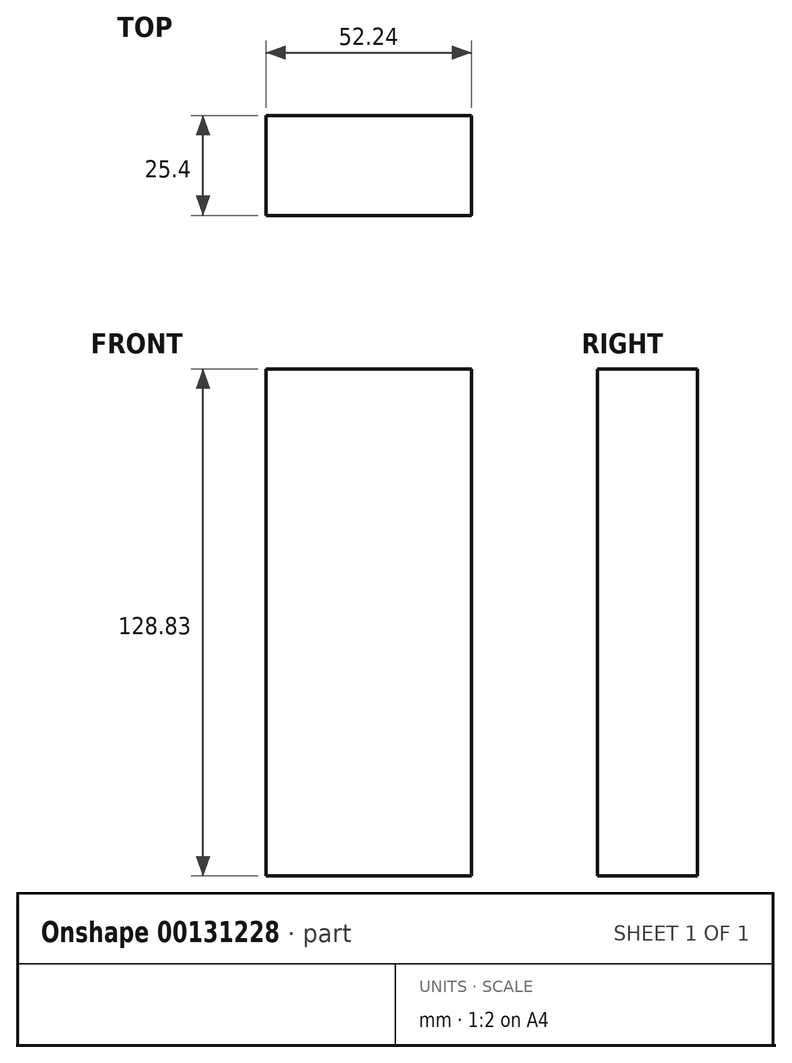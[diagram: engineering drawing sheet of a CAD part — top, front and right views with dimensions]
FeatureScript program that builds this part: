
annotation { "Feature Type Name" : "Feature", "Feature Type Description" : "" }
export const myFeature = defineFeature(function(context is Context, id is Id, definition is map)
    precondition{}
    {
        {
            var Q0;
            Q0=qCreatedBy(makeId("Front.planeOp"),FACE);
            var sketch = newSketch(context, id + "F0", { "sketchPlane" : qUnion([Q0])});
            skLineSegment(sketch, "E0.bottom", {"start": v(-30.38, -8.5) * mm, "end": v(-82.62, -8.5) * mm});
            skLineSegment(sketch, "E0.top", {"start": v(-30.38, 120.33) * mm, "end": v(-82.62, 120.33) * mm});
            skLineSegment(sketch, "E0.left", {"start": v(-30.38, -8.5) * mm, "end": v(-30.38, 120.33) * mm});
            skLineSegment(sketch, "E0.right", {"start": v(-82.62, -8.5) * mm, "end": v(-82.62, 120.33) * mm});
            skPoint(sketch, "E0.middle", {"position": v(-56.5, 55.91) * mm});
            skLineSegment(sketch, "E1.bottom", {"start": v(15.98, -28.7) * mm, "end": v(-4.11, -28.7) * mm});
            skLineSegment(sketch, "E1.top", {"start": v(15.98, 110.48) * mm, "end": v(-4.11, 110.48) * mm});
            skLineSegment(sketch, "E1.left", {"start": v(15.98, -28.7) * mm, "end": v(15.98, 110.48) * mm});
            skLineSegment(sketch, "E1.right", {"start": v(-4.11, -28.7) * mm, "end": v(-4.11, 110.48) * mm});
            skPoint(sketch, "E1.middle", {"position": v(5.94, 40.89) * mm});
            skSolve(sketch);
        }
        {
            var Q0;
            Q0=makeQuery(id+"F0.imprint","IMPRINT",FACE,{"disambiguationData":[TD([[makeQuery(id+"F0.imprint","IMPRINT",EDGE,{"derivedFrom":sQuery(id+"F0.wireOp",EDGE,"E0.bottom")}),-1.0]])]});
            extrude(context, id + "F1", {"entities" : qUnion([Q0]), "depth" : 25.4 * mm});
        }
    });
